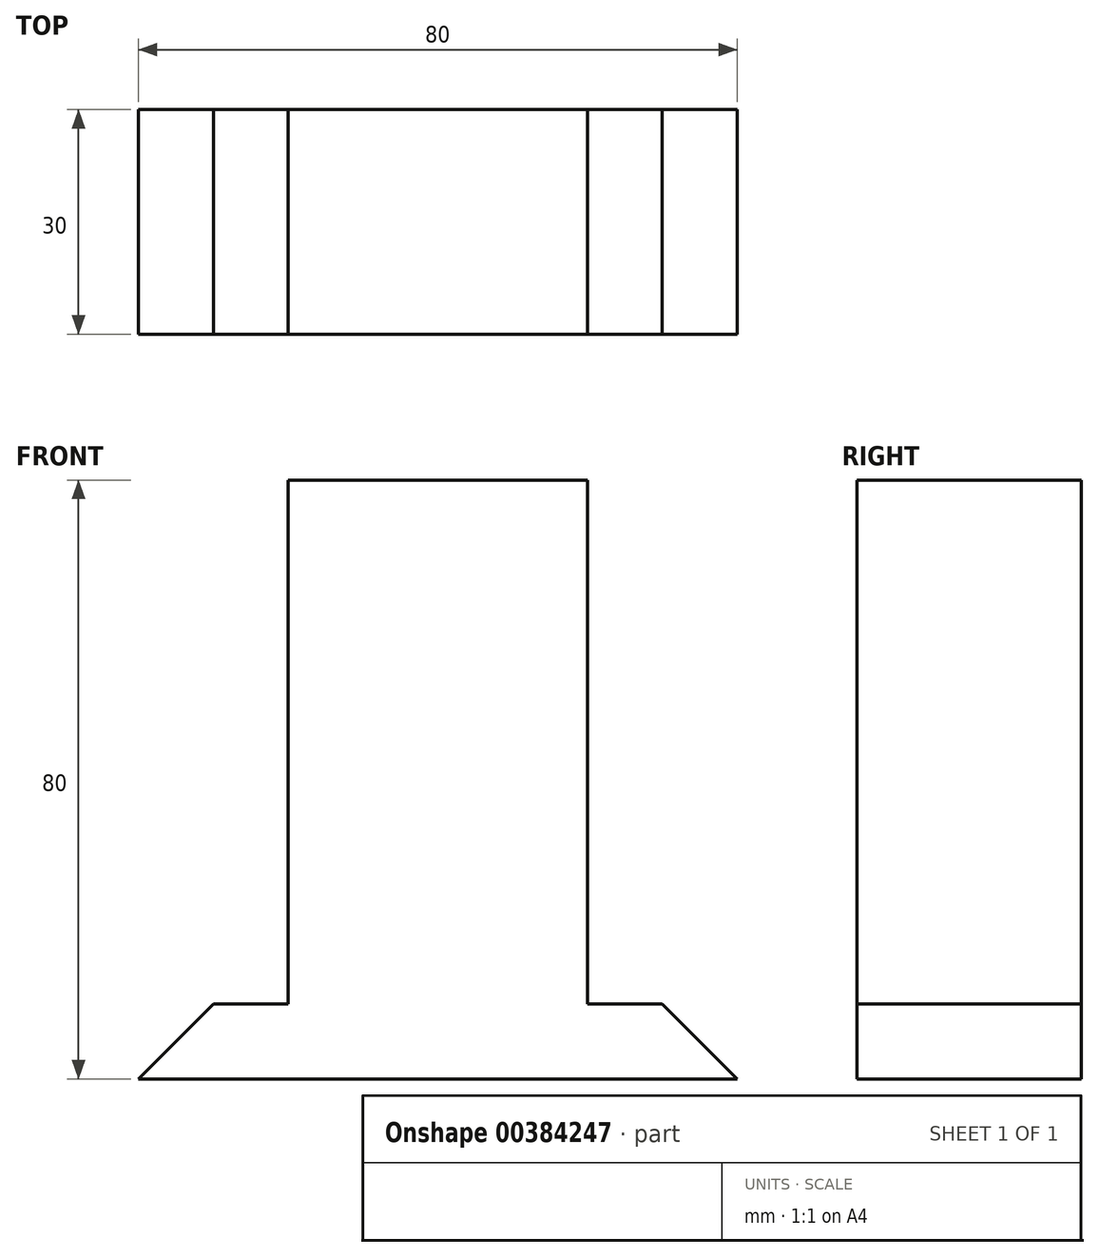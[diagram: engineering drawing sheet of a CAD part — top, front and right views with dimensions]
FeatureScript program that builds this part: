
annotation { "Feature Type Name" : "Feature", "Feature Type Description" : "" }
export const myFeature = defineFeature(function(context is Context, id is Id, definition is map)
    precondition{}
    {
        {
            var Q0;
            Q0=qCreatedBy(makeId("Top.planeOp"),FACE);
            var sketch = newSketch(context, id + "F0", { "sketchPlane" : qUnion([Q0])});
            skLineSegment(sketch, "E0.bottom", {"start": v(40, -15) * mm, "end": v(-40, -15) * mm});
            skLineSegment(sketch, "E0.top", {"start": v(40, 15) * mm, "end": v(-40, 15) * mm});
            skLineSegment(sketch, "E0.left", {"start": v(40, -15) * mm, "end": v(40, 15) * mm});
            skLineSegment(sketch, "E0.right", {"start": v(-40, -15) * mm, "end": v(-40, 15) * mm});
            skPoint(sketch, "E0.middle", {"position": v(0, 0) * mm});
            skSolve(sketch);
        }
        {
            var Q0;
            Q0=makeQuery(id+"F0.imprint","IMPRINT",FACE,{"disambiguationData":[TD([[makeQuery(id+"F0.imprint","IMPRINT",EDGE,{"derivedFrom":sQuery(id+"F0.wireOp",EDGE,"E0.bottom")}),-1.0]])]});
            extrude(context, id + "F1", {"entities" : qUnion([Q0]), "depth" : 10 * mm});
        }
        {
            var Q0;
            Q0=makeQuery(id+"F1.opExtrude","CAP_EDGE",EDGE,{"disambiguationData":[OSD([sQuery(id+"F0.wireOp",EDGE,"E0.left")])],"isStart":false});
            var Q1;
            Q1=makeQuery(id+"F1.opExtrude","CAP_EDGE",EDGE,{"disambiguationData":[OSD([sQuery(id+"F0.wireOp",EDGE,"E0.right")])],"isStart":false});
            chamfer(context, id + "F2", {"entities" : qUnion([Q0, Q1]), "width" : 10 * mm, "tangentPropagation" : true});
        }
        {
            var Q0;
            Q0=qCreatedBy(makeId("Top.planeOp"),FACE);
            var sketch = newSketch(context, id + "F3", { "sketchPlane" : qUnion([Q0])});
            skLineSegment(sketch, "E1.left", {"start": v(20, 15) * mm, "end": v(16.3, -17.03) * mm});
            skLineSegment(sketch, "E1.right", {"start": v(-16.3, 17.03) * mm, "end": v(-20, -15) * mm});
            skPoint(sketch, "E1.middle", {"position": v(0, 0) * mm});
            skLineSegment(sketch, "E2.bottom", {"start": v(20, 15) * mm, "end": v(-20, 15) * mm});
            skLineSegment(sketch, "E2.top", {"start": v(20, -15) * mm, "end": v(-20, -15) * mm});
            skLineSegment(sketch, "E2.left", {"start": v(20, 15) * mm, "end": v(20, -15) * mm});
            skLineSegment(sketch, "E2.right", {"start": v(-20, 15) * mm, "end": v(-20, -15) * mm});
            skSolve(sketch);
        }
        {
            var Q0;
            Q0 = qSketchRegion(id + "F3", true);
            extrude(context, id + "F4", {"entities" : qUnion([Q0]), "operationType" : NewBodyOperationType.ADD, "depth" : 40 * mm});
        }
        {
            var Q0;
            Q0 = qSketchRegion(id + "F3", true);
            var Q1;
            Q1=makeQuery(id+"F4.opExtrude","CAP_FACE",FACE,{"disambiguationData":[OSD([sQuery(id+"F3.wireOp",EDGE,"E2.bottom"),sQuery(id+"F3.wireOp",EDGE,"E2.top"),sQuery(id+"F3.wireOp",EDGE,"E2.left"),sQuery(id+"F3.wireOp",EDGE,"E2.right")])],"isStart":false});
            extrude(context, id + "F5", {"entities" : qUnion([Q0, Q1]), "operationType" : NewBodyOperationType.ADD, "depth" : 40 * mm});
        }
    });
